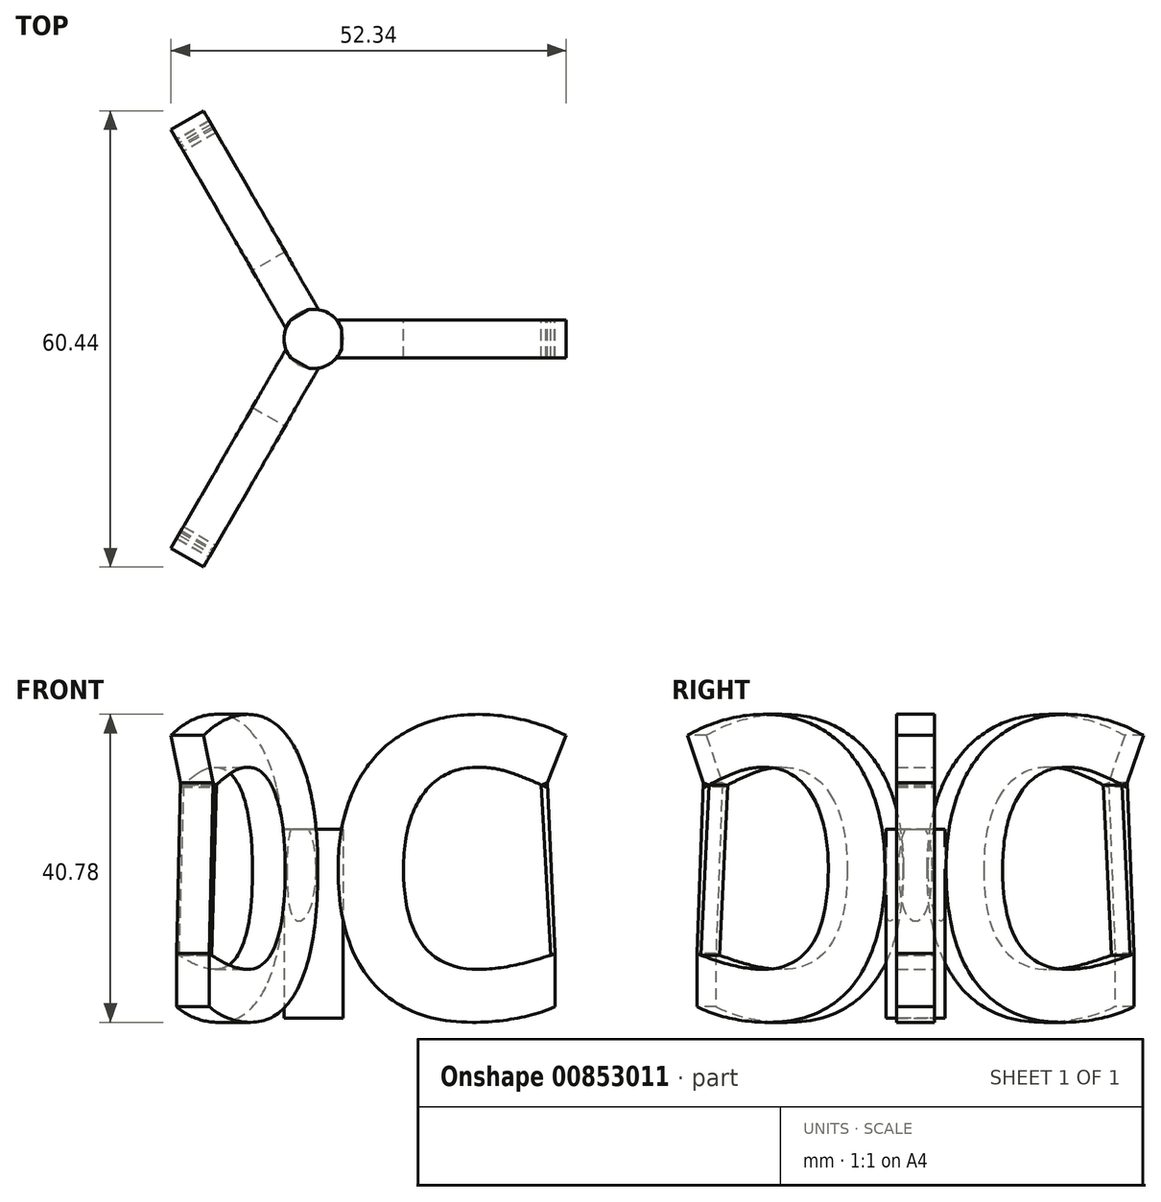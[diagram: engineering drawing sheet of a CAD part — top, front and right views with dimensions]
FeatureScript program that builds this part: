
annotation { "Feature Type Name" : "Feature", "Feature Type Description" : "" }
export const myFeature = defineFeature(function(context is Context, id is Id, definition is map)
    precondition{}
    {
        {
            var Q0;
            Q0=qCreatedBy(makeId("Front.planeOp"),FACE);
            var sketch = newSketch(context, id + "F0", { "sketchPlane" : qUnion([Q0])});
            skText(sketch, "E0", { "text": "C", "fontName": "OpenSans-Bold.ttf"});
            skLineSegment(sketch, "E1", {"start": v(30.97, 31.18) * mm, "end": v(31.95, 8.54) * mm});
            skLineSegment(sketch, "E2", {"start": v(30.97, 31.18) * mm, "end": v(30.13, 30.87) * mm});
            skLineSegment(sketch, "E3", {"start": v(30.13, 30.87) * mm, "end": v(31.39, 8.33) * mm});
            skLineSegment(sketch, "E4", {"start": v(31.39, 8.33) * mm, "end": v(31.95, 8.54) * mm});
            const initialGuessF0  = {"E0": [0, 0, 1, 0, 0.04]};
            skSetInitialGuess(sketch, initialGuessF0);
            skSolve(sketch);
        }
        {
            var Q0;
            Q0=makeQuery(id+"F0.imprint","IMPRINT",FACE,{"disambiguationData":[TD([[makeQuery(id+"F0.imprint","IMPRINT",EDGE,{"derivedFrom":sQuery(id+"F0.wireOp",EDGE,"a16f313e-8ab7-412c-a768-1ef7773b63e5.sketch_text.stroke-0")}),-1.0]])]});
            var Q1;
            Q1=makeQuery(id+"F0.imprint","IMPRINT",FACE,{"disambiguationData":[TD([[makeQuery(id+"F0.imprint","IMPRINT",EDGE,{"derivedFrom":sQuery(id+"F0.wireOp",EDGE,"E0.sketch_text.stroke-0")}),-1.0]])]});
            var Q2;
            Q2=makeQuery(id+"F0.imprint","IMPRINT",FACE,{"disambiguationData":[TD([[makeQuery(id+"F0.imprint","IMPRINT",EDGE,{"derivedFrom":sQuery(id+"F0.wireOp",EDGE,"E1")}),-1.0]])]});
            extrude(context, id + "F1", {"entities" : qUnion([Q0, Q1, Q2]), "endBound" : BoundingType.SYMMETRIC, "depth" : 5 * mm, "offsetDistance" : 25 * mm});
        }
        {
            var Q0;
            Q0=qCreatedBy(makeId("Top.planeOp"),FACE);
            var sketch = newSketch(context, id + "F2", { "sketchPlane" : qUnion([Q0])});
            skCircle(sketch, "E5", {"center": v(0, 0) * mm, "radius": 3.93 * mm});
            skSolve(sketch);
        }
        {
            var Q0;
            Q0 = qSketchRegion(id + "F2", true);
            extrude(context, id + "F3", {"entities" : qUnion([Q0]), "operationType" : NewBodyOperationType.ADD, "depth" : 25 * mm, "offsetDistance" : 25 * mm});
        }
        {
            var Q0;
            Q0=makeQuery(id+"F1.opExtrude","SWEPT_BODY",BODY,{"disambiguationData":[OSD([sQuery(id+"F0.wireOp",EDGE,"E0.sketch_text.stroke-0"),sQuery(id+"F0.wireOp",EDGE,"E0.sketch_text.stroke-1"),sQuery(id+"F0.wireOp",EDGE,"E0.sketch_text.stroke-2"),sQuery(id+"F0.wireOp",EDGE,"E0.sketch_text.stroke-3"),sQuery(id+"F0.wireOp",EDGE,"E0.sketch_text.stroke-4"),sQuery(id+"F0.wireOp",EDGE,"E0.sketch_text.stroke-5"),sQuery(id+"F0.wireOp",EDGE,"E0.sketch_text.stroke-6"),sQuery(id+"F0.wireOp",EDGE,"E0.sketch_text.stroke-7"),sQuery(id+"F0.wireOp",EDGE,"E0.sketch_text.stroke-8"),sQuery(id+"F0.wireOp",EDGE,"E0.sketch_text.stroke-9"),sQuery(id+"F0.wireOp",EDGE,"E0.sketch_text.stroke-10"),sQuery(id+"F0.wireOp",EDGE,"E0.sketch_text.stroke-11"),sQuery(id+"F0.wireOp",EDGE,"E0.sketch_text.stroke-12"),sQuery(id+"F0.wireOp",EDGE,"E0.sketch_text.stroke-13"),sQuery(id+"F0.wireOp",EDGE,"E0.sketch_text.stroke-14")])]});
            var Q1;
            Q1=makeQuery(id+"F3.opExtrude","SWEPT_FACE",FACE,{"disambiguationData":[OSD([sQuery(id+"F2.wireOp",EDGE,"E5")])]});
            circularPattern(context, id + "F4", {"entities" : qUnion([Q0]), "axis" : qUnion([Q1]), "angle" : 360 * degree, "instanceCount" : 3, "equalSpace" : true});
        }
        {
            var Q0;
            Q0=makeQuery(id+"F1.opExtrude","SWEPT_BODY",BODY,{"disambiguationData":[OSD([sQuery(id+"F0.wireOp",EDGE,"E1"),sQuery(id+"F0.wireOp",EDGE,"E2"),sQuery(id+"F0.wireOp",EDGE,"E3"),sQuery(id+"F0.wireOp",EDGE,"E4")])]});
            var Q1;
            Q1=makeQuery(id+"F3.opExtrude","SWEPT_FACE",FACE,{"disambiguationData":[OSD([sQuery(id+"F2.wireOp",EDGE,"E5")])]});
            circularPattern(context, id + "F5", {"entities" : qUnion([Q0]), "axis" : qUnion([Q1]), "angle" : 360 * degree, "instanceCount" : 3, "equalSpace" : true});
        }
    });
